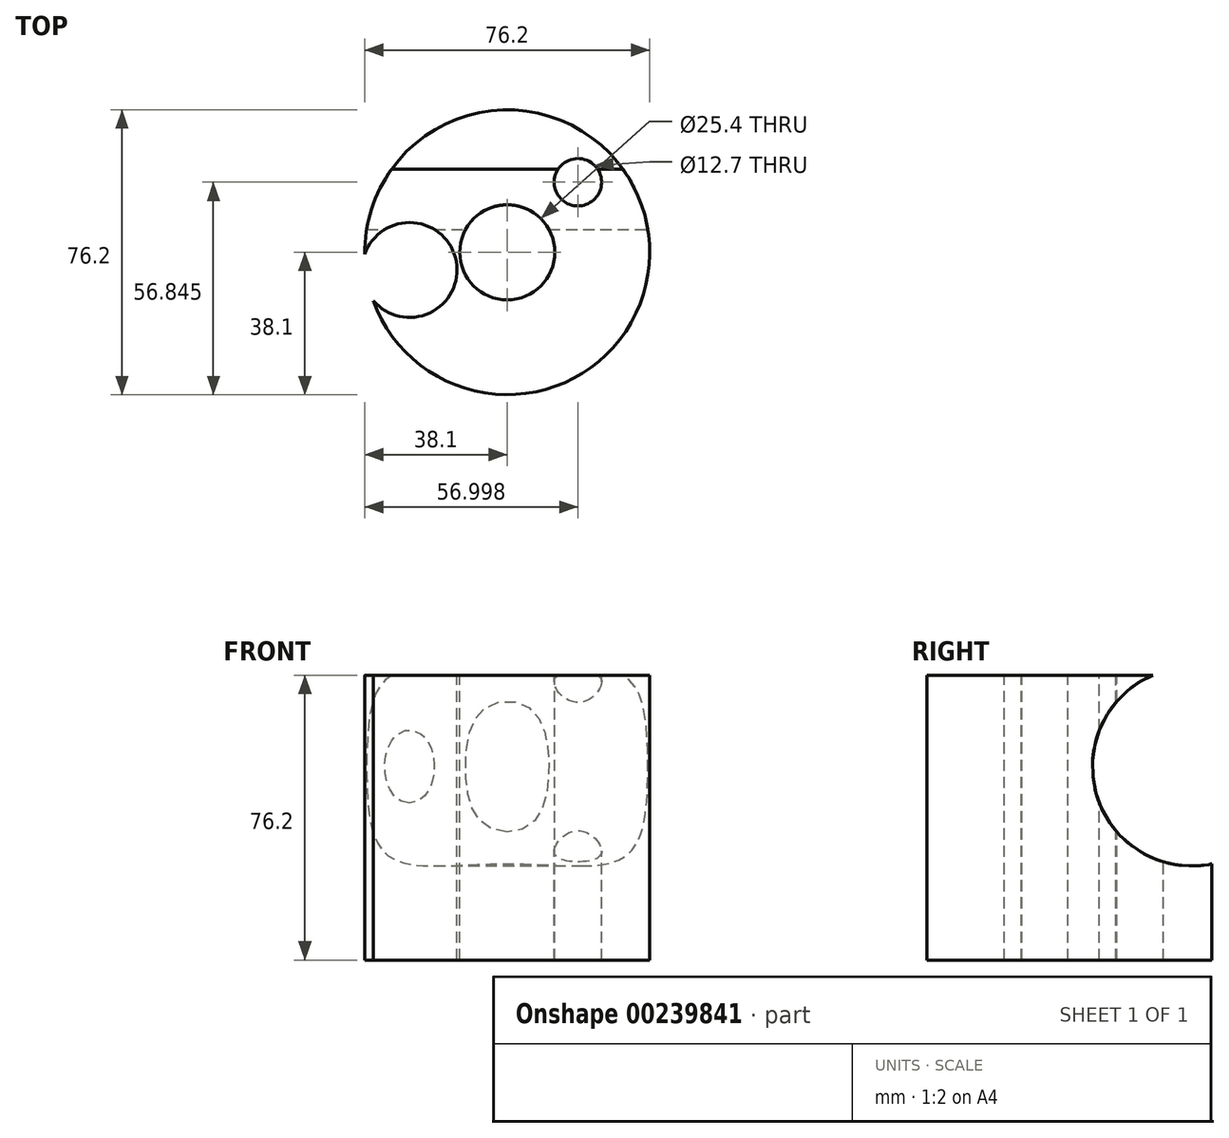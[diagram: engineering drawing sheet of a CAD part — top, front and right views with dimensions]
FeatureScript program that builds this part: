
annotation { "Feature Type Name" : "Feature", "Feature Type Description" : "" }
export const myFeature = defineFeature(function(context is Context, id is Id, definition is map)
    precondition{}
    {
        {
            var Q0;
            Q0=qCreatedBy(makeId("Top.planeOp"),FACE);
            var sketch = newSketch(context, id + "F0", { "sketchPlane" : qUnion([Q0])});
            skCircle(sketch, "E0", {"center": v(0, 0) * mm, "radius": 38.1 * mm});
            skSolve(sketch);
        }
        {
            var Q0;
            Q0=makeQuery(id+"F0.imprint","IMPRINT",FACE,{"disambiguationData":[TD([[makeQuery(id+"F0.imprint","IMPRINT",EDGE,{"derivedFrom":sQuery(id+"F0.wireOp",EDGE,"E0")}),1.0]])]});
            extrude(context, id + "F1", {"entities" : qUnion([Q0]), "depth" : 76.2 * mm});
        }
        {
            var Q0;
            Q0=makeQuery(id+"F1.opExtrude","CAP_FACE",FACE,{"disambiguationData":[OSD([sQuery(id+"F0.wireOp",EDGE,"E0")])],"isStart":false});
            var sketch = newSketch(context, id + "F2", { "sketchPlane" : qUnion([Q0])});
            skCircle(sketch, "E1", {"center": v(0, 0) * mm, "radius": 12.7 * mm});
            skSolve(sketch);
        }
        {
            var Q0;
            Q0=makeQuery(id+"F2.imprint","IMPRINT",FACE,{"disambiguationData":[TD([[makeQuery(id+"F2.imprint","IMPRINT",EDGE,{"derivedFrom":sQuery(id+"F2.wireOp",EDGE,"E1")}),1.0]])]});
            extrude(context, id + "F3", {"entities" : qUnion([Q0]), "operationType" : NewBodyOperationType.REMOVE, "oppositeDirection" : true, "depth" : 255.78 * mm});
        }
        {
            var Q0;
            Q0=makeQuery(id+"F1.opExtrude","CAP_FACE",FACE,{"disambiguationData":[OSD([sQuery(id+"F0.wireOp",EDGE,"E0")])],"isStart":false});
            var sketch = newSketch(context, id + "F4", { "sketchPlane" : qUnion([Q0])});
            skCircle(sketch, "E2", {"center": v(18.9, 18.75) * mm, "radius": 6.35 * mm});
            skSolve(sketch);
        }
        {
            var Q0;
            Q0=makeQuery(id+"F4.imprint","IMPRINT",FACE,{"disambiguationData":[TD([[makeQuery(id+"F4.imprint","IMPRINT",EDGE,{"derivedFrom":sQuery(id+"F4.wireOp",EDGE,"E2")}),1.0]])]});
            extrude(context, id + "F5", {"entities" : qUnion([Q0]), "operationType" : NewBodyOperationType.REMOVE, "oppositeDirection" : true, "depth" : 105.16 * mm});
        }
        {
            var Q0;
            Q0=makeQuery(id+"F1.opExtrude","CAP_FACE",FACE,{"disambiguationData":[OSD([sQuery(id+"F0.wireOp",EDGE,"E0")])],"isStart":false});
            var sketch = newSketch(context, id + "F6", { "sketchPlane" : qUnion([Q0])});
            skSolve(sketch);
        }
        {
            var Q0;
            Q0=makeQuery(id+"F6.imprint","IMPRINT",FACE,{"disambiguationData":[TD([[makeQuery(id+"F6.imprint","IMPRINT",EDGE,{"derivedFrom":makeQuery(id+"F1.opExtrude","CAP_EDGE",EDGE,{"disambiguationData":[OSD([sQuery(id+"F0.wireOp",EDGE,"E0")])],"isStart":false})}),1.0]])]});
            var sketch = newSketch(context, id + "F7", { "sketchPlane" : qUnion([Q0])});
            skCircle(sketch, "E3", {"center": v(-26.13, -4.72) * mm, "radius": 12.7 * mm});
            skSolve(sketch);
        }
        {
            var Q0;
            Q0 = qSketchRegion(id + "F7", true);
            extrude(context, id + "F8", {"entities" : qUnion([Q0]), "operationType" : NewBodyOperationType.REMOVE, "oppositeDirection" : true, "depth" : 112.52 * mm});
        }
        {
            var Q0;
            Q0=qCreatedBy(makeId("Right.planeOp"),FACE);
            var sketch = newSketch(context, id + "F9", { "sketchPlane" : qUnion([Q0])});
            skCircle(sketch, "E4", {"center": v(32.7, 51.74) * mm, "radius": 26.57 * mm});
            skCircle(sketch, "E5", {"center": v(59.24, 50.65) * mm, "radius": 16.32 * mm});
            skSolve(sketch);
        }
        {
            var Q0;
            Q0 = qSketchRegion(id + "F9", true);
            extrude(context, id + "F10", {"entities" : qUnion([Q0]), "operationType" : NewBodyOperationType.REMOVE, "endBound" : BoundingType.SYMMETRIC, "oppositeDirection" : true, "depth" : 183.39 * mm});
        }
    });
